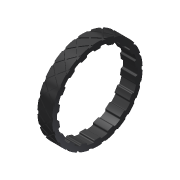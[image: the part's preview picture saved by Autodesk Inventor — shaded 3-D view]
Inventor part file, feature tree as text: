
AUTODESK INVENTOR PART (.ipt)
format: ipt  version: 2013 (Build 170138000, 138)  size: 1,055,232 bytes
history: native  units: in
note: dims shown in document units (in); Inventor stores cm internally (conversion verified against a paired STEP export)
features: pattern_circular x1, extrude x1, mirror x1, imported_body x1, sketch x1
ambient origin geometry x8: Origin, YZ Plane, XZ Plane, XY Plane, X Axis, Y Axis, Z Axis, Center Point
feature tree (5):
  pattern_circular  "CirPattern3"
  extrude  "Extrusion1"  Depth=0.5in TaperAngle=0.0deg
  mirror  "Mirror1"
  imported_body  "Base1"
  sketch  "Sketch1"  dims[d0=6.5in d1=0.5in d2=0.0in]
